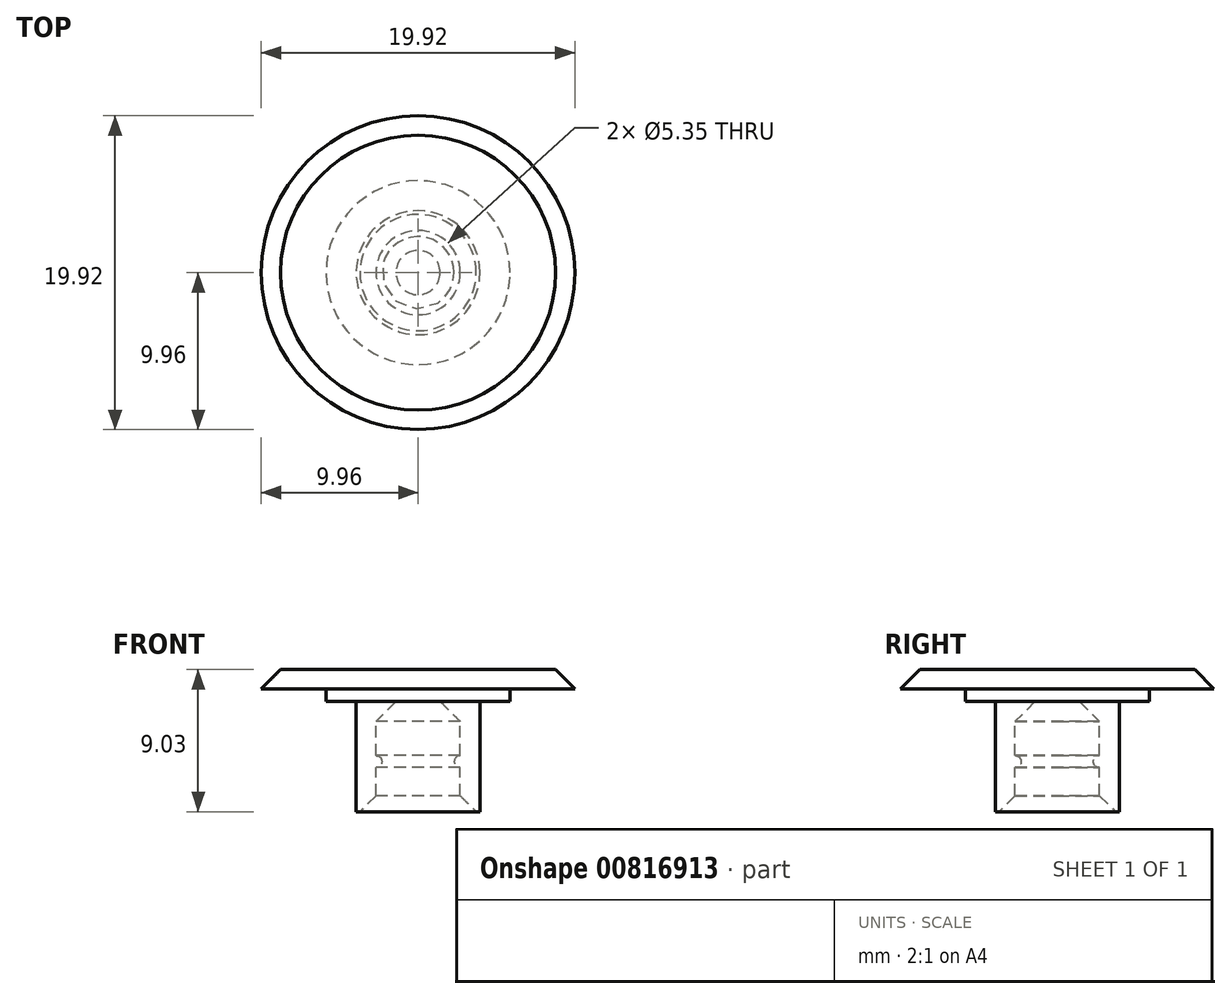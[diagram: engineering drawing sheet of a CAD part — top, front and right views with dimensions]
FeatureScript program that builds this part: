
annotation { "Feature Type Name" : "Feature", "Feature Type Description" : "" }
export const myFeature = defineFeature(function(context is Context, id is Id, definition is map)
    precondition{}
    {
        {
            var Q0;
            Q0=qCreatedBy(makeId("Front.planeOp"),FACE);
            var sketch = newSketch(context, id + "F0", { "sketchPlane" : qUnion([Q0])});
            skLineSegment(sketch, "E0", {"start": v(2.68, 0) * mm, "end": v(2.68, -3.44) * mm});
            skLineSegment(sketch, "E1", {"start": v(2.68, -7) * mm, "end": v(3.94, -7) * mm});
            skLineSegment(sketch, "E2", {"start": v(3.94, -7) * mm, "end": v(3.94, 0) * mm});
            skLineSegment(sketch, "E3", {"start": v(3.94, 0) * mm, "end": v(10, 0) * mm});
            skLineSegment(sketch, "E4", {"start": v(10, 0) * mm, "end": v(10, 2.03) * mm});
            skLineSegment(sketch, "E5", {"start": v(0, 2.03) * mm, "end": v(0, 0) * mm});
            skLineSegment(sketch, "E6", {"start": v(0, 0) * mm, "end": v(2.68, 0) * mm});
            skArc(sketch, "E7", {"start": v(2.68, -3.44) * mm, "mid": v(2.3, -3.82) * mm, "end": v(2.68, -4.2) * mm});
            skLineSegment(sketch, "E8.trimOffspring", {"start": v(2.68, -4.2) * mm, "end": v(2.68, -7) * mm});
            skLineSegment(sketch, "E9", {"start": v(0, 2.03) * mm, "end": v(10, 2.03) * mm});
            skPoint(sketch, "E10.center.orphan", {"position": v(0, 15.24) * mm});
            skSolve(sketch);
        }
        {
            var Q0;
            Q0=qSketchRegion(id+"F0",true);
            var Q1;
            Q1=sQuery(id+"F0.wireOp",EDGE,"E5");
            revolve(context, id + "F1", {"surfaceOperationType" : NewSurfaceOperationType.NEW, "entities" : qUnion([Q0]), "axis" : qUnion([Q1]), "revolveType" : RevolveType.FULL});
        }
        {
            var Q0;
            Q0=makeQuery(id+"F1.opRevolve","SWEPT_EDGE",EDGE,{"disambiguationData":[OSD([sQuery(id+"F0.wireOp",EDGE,"E0"),sQuery(id+"F0.wireOp",EDGE,"E6")])]});
            chamfer(context, id + "F2", {"entities" : qUnion([Q0]), "width" : 1.27 * mm, "tangentPropagation" : true});
        }
        {
            var Q0;
            Q0=makeQuery(id+"F1.opRevolve","SWEPT_FACE",FACE,{"disambiguationData":[OSD([sQuery(id+"F0.wireOp",EDGE,"E3")])]});
            var sketch = newSketch(context, id + "F3", { "sketchPlane" : qUnion([Q0])});
            skCircle(sketch, "E11", {"center": v(0, 0) * mm, "radius": 5.84 * mm});
            skCircle(sketch, "E12", {"center": v(0, -0.88) * mm, "radius": 18.96 * mm});
            skSolve(sketch);
        }
        {
            var Q0;
            Q0=qSketchRegion(id+"F3",true);
            extrude(context, id + "F4", {"entities" : qUnion([Q0]), "operationType" : NewBodyOperationType.REMOVE, "oppositeDirection" : true, "depth" : .8 * mm, "offsetDistance" : 25.4 * mm});
        }
        {
            var Q0;
            Q0=makeQuery(id+"F1.opRevolve","SWEPT_EDGE",EDGE,{"disambiguationData":[OSD([sQuery(id+"F0.wireOp",EDGE,"E1"),sQuery(id+"F0.wireOp",EDGE,"E8.trimOffspring")])]});
            chamfer(context, id + "F5", {"entities" : qUnion([Q0]), "width" : 1.02 * mm, "tangentPropagation" : true});
        }
        {
            var Q0;
            Q0=makeQuery(id+"F1.opRevolve","SWEPT_EDGE",EDGE,{"disambiguationData":[OSD([sQuery(id+"F0.wireOp",EDGE,"E4"),sQuery(id+"F0.wireOp",EDGE,"E9")])]});
            chamfer(context, id + "F6", {"entities" : qUnion([Q0]), "width" : 1.27 * mm, "tangentPropagation" : true});
        }
    });
